# Revit family: Storage-Teknion-MXCEV-Elevated_Credenza_Ventilated-Expansion_Meeting-R2023
name_source: partatom
category: Furniture
units: mm (PartAtom-declared; Revit-internal decimal feet)

## family parameters
Always vertical = Yes
Cut with Voids When Loaded = No
Enable Cutting in Views = No
OmniClass Number = 23.40.20.00
OmniClass Title = General Furniture and Specialties
Render Appearance Source = Family Geometry
Room Calculation Point = No
Shared = Yes
Work Plane-Based = No

## types (6) — shared parameters
Assembly Code = E2020200
Blade Foot 30-48 = No
Depth = 24 "
Door H = 28.323 "
Height = 36 "
Manufacturer = Teknion
Manufacturer Fax = 416.661.4586
Mid Vent 1 = No
Mid Vent 4 = No
Part Number = MXCEV
Product Documentation Link = http://www.teknion.com
Product Line = Credenzas
Product Page URL = http://www.teknion.com
Series = Meeting Expansion
Shelf 1 = No
Shelf 1 Dim = 8.416 "
Sustainability Data = https://www.teknion.com
URL = www.teknion.com
Unit Weight URL = http://www.teknion.com
Warranty = http://www.teknion.com
zero-valued in all types: Default Elevation

## per-type parameters (varying)
| type | 1 Pull-Out Bin | 2 Pull-Out Bins | Bin 1 | Bin 2 | Bin 2 Dim | Bin Shelf | Bin Shelf Dim | Blade Foot | Blade Foot 54+ | Blade Foot Dim | Description | Door Dim | Door Width | Mid Shelf | Mid Vent 2 | Mid Vent 3 | Model | No Pull-Out Bin | Shelf 2 | Shelf 3 Dim | Shelves | Shelves Dim | Square Foot | Width |
| No Pull-Out Bin / Square Foot | No | No | No | No | 27.175 " | No | 18.35 " | No | No | 10.296 " | Meeting Expansion, Elevated Credenzas Ventilated - No Pull-Out Bin | 17.532 " | 4 | Yes | No | No | MXCEVS______N | Yes | No | 0 " | No | 15.46 " | Yes | 72 " |
| 1 Pull-Out Bin / Blade Foot | Yes | No | Yes | No | 22.675 " | Yes | 15.35 " | Yes | Yes | 8.58 " | Meeting Expansion, Elevated Credenzas Ventilated - 1 Pull-Out Bin | 14.532 " | 4 | Yes | No | Yes | MXCEVB______R / MXCEVB______L | No | No | 14.649 " | No | 15.46 " | No | 60 " |
| 2 Pull-Out Bins / Square Foot | No | Yes | Yes | Yes | 24.35 " | Yes | 16.467 " | No | No | 13.728 " | Meeting Expansion, Elevated Credenzas Ventilated - 2 Pull-Out Bins | 15.648 " | 6 | No | Yes | No | MXCEVS______T / MXCEVS______V | No | Yes | 31.416 " | Yes | 31.766 " | Yes | 96 " |
| 2 Pull-Out Bins / Blade Foot | No | Yes | Yes | Yes | 24.35 " | Yes | 16.467 " | Yes | Yes | 13.728 " | Meeting Expansion, Elevated Credenzas Ventilated - 2 Pull-Out Bins | 15.648 " | 6 | No | Yes | No | MXCEVB______T / MXCEVB______V | No | Yes | 31.416 " | Yes | 31.766 " | No | 96 " |
| 1 Pull-Out Bin / Square Foot | Yes | No | Yes | No | 24.35 " | Yes | 16.467 " | No | No | 13.728 " | Meeting Expansion, Elevated Credenzas Ventilated - 1 Pull-Out Bin | 15.648 " | 6 | No | Yes | Yes | MXCEVS______R / MXCEVS______L | No | Yes | 15.766 " | Yes | 31.766 " | Yes | 96 " |
| No Pull-Out Bin / Blade Foot | No | No | No | No | 27.175 " | No | 18.35 " | Yes | Yes | 10.296 " | Meeting Expansion, Elevated Credenzas Ventilated - No Pull-Out Bin | 17.532 " | 4 | Yes | No | No | MXCEVB______N | Yes | No | 0 " | No | 15.46 " | No | 72 " |

## geometry (parser evidence)
native form markers: Sweep x2
no freeform markers — native parametric forms only
